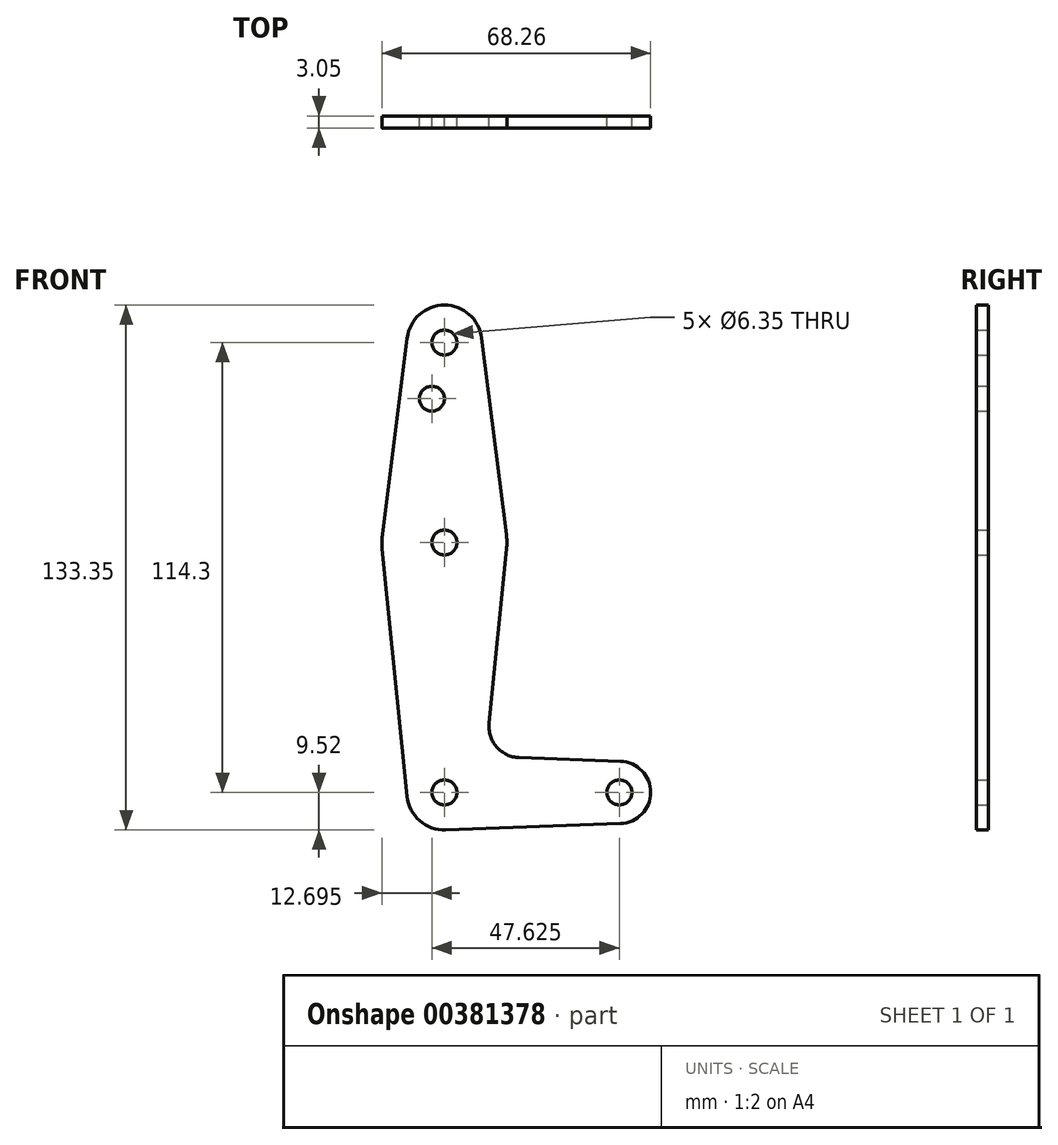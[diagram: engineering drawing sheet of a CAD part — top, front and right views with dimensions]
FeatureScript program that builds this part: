
annotation { "Feature Type Name" : "Feature", "Feature Type Description" : "" }
export const myFeature = defineFeature(function(context is Context, id is Id, definition is map)
    precondition{}
    {
        {
            var Q0;
            Q0=qCreatedBy(makeId("Front.planeOp"),FACE);
            var sketch = newSketch(context, id + "F0", { "sketchPlane" : qUnion([Q0])});
            skLineSegment(sketch, "E0", {"start": v(0, 0) * mm, "end": v(0, 114.3) * mm, "construction": true});
            skLineSegment(sketch, "E1", {"start": v(0, 0) * mm, "end": v(44.45, 0) * mm, "construction": true});
            skCircle(sketch, "E2", {"center": v(0, 114.3) * mm, "radius": 9.53 * mm});
            skCircle(sketch, "E3", {"center": v(0, 63.5) * mm, "radius": 15.88 * mm});
            skCircle(sketch, "E4", {"center": v(0, 0) * mm, "radius": 9.53 * mm});
            skCircle(sketch, "E5", {"center": v(44.45, 0) * mm, "radius": 7.94 * mm});
            skLineSegment(sketch, "E6", {"start": v(-9.45, 115.5) * mm, "end": v(-15.75, 65.48) * mm});
            skLineSegment(sketch, "E7", {"start": v(9.45, 115.5) * mm, "end": v(15.75, 65.48) * mm});
            skCircle(sketch, "E8", {"center": v(0, 114.3) * mm, "radius": 3.18 * mm});
            skCircle(sketch, "E9", {"center": v(0, 63.5) * mm, "radius": 3.18 * mm});
            skCircle(sketch, "E10", {"center": v(0, 0) * mm, "radius": 3.18 * mm});
            skCircle(sketch, "E11", {"center": v(44.45, 0) * mm, "radius": 3.18 * mm});
            skCircle(sketch, "E12", {"center": v(-3.18, 100.03) * mm, "radius": 3.18 * mm});
            skLineSegment(sketch, "E13", {"start": v(44.73, 7.93) * mm, "end": v(18.97, 8.85) * mm});
            skLineSegment(sketch, "E14", {"start": v(15.8, 61.91) * mm, "end": v(11.34, 17.6) * mm});
            skArc(sketch, "E15.filletArc", {"start": v(11.34, 17.6) * mm, "mid": v(13.26, 11.57) * mm, "end": v(18.97, 8.85) * mm});
            skLineSegment(sketch, "E16", {"start": v(0.34, -9.52) * mm, "end": v(44.73, -7.93) * mm});
            skLineSegment(sketch, "E17", {"start": v(-15.8, 61.91) * mm, "end": v(-9.48, -0.95) * mm});
            skSolve(sketch);
        }
        {
            var Q0;
            Q0 = qSketchRegion(id + "F0", true);
            extrude(context, id + "F1", {"entities" : qUnion([Q0]), "depth" : 3.05 * mm});
        }
    });
